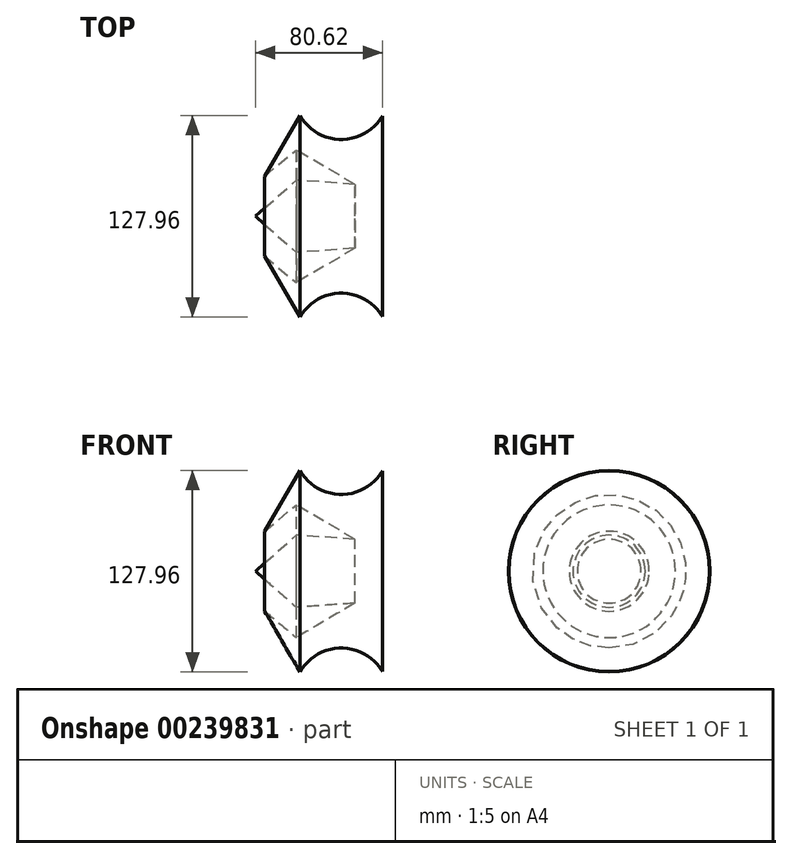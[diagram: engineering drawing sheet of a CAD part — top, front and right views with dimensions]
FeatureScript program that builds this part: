
annotation { "Feature Type Name" : "Feature", "Feature Type Description" : "" }
export const myFeature = defineFeature(function(context is Context, id is Id, definition is map)
    precondition{}
    {
        {
            var Q0;
            Q0=qCreatedBy(makeId("Top.planeOp"),FACE);
            var sketch = newSketch(context, id + "F0", { "sketchPlane" : qUnion([Q0])});
            skLineSegment(sketch, "E0", {"start": v(0, 0) * mm, "end": v(-80.62, 0) * mm});
            skLineSegment(sketch, "E1", {"start": v(-80.62, 0) * mm, "end": v(-54.64, 22.95) * mm});
            skLineSegment(sketch, "E2", {"start": v(-54.64, 22.95) * mm, "end": v(-17.48, 20.28) * mm});
            skLineSegment(sketch, "E3", {"start": v(-17.48, 20.28) * mm, "end": v(-54.64, 42.13) * mm});
            skLineSegment(sketch, "E4", {"start": v(-54.64, 42.13) * mm, "end": v(-74.79, 25.37) * mm});
            skLineSegment(sketch, "E5", {"start": v(-74.79, 25.37) * mm, "end": v(-52.45, 63.98) * mm});
            skLineSegment(sketch, "E6", {"start": v(0, 0) * mm, "end": v(0, 63.74) * mm});
            skArc(sketch, "E7", {"start": v(-52.45, 63.98) * mm, "mid": v(-26.3, 48.8) * mm, "end": v(0, 63.74) * mm});
            skSolve(sketch);
        }
        {
            var Q0;
            Q0=makeQuery(id+"F0.imprint","IMPRINT",FACE,{"disambiguationData":[TD([[makeQuery(id+"F0.imprint","IMPRINT",EDGE,{"derivedFrom":sQuery(id+"F0.wireOp",EDGE,"E0")}),-1.0]])]});
            var Q1;
            Q1=sQuery(id+"F0.wireOp",EDGE,"E0");
            revolve(context, id + "F1", {"entities" : qUnion([Q0]), "axis" : qUnion([Q1]), "revolveType" : RevolveType.FULL});
        }
    });
